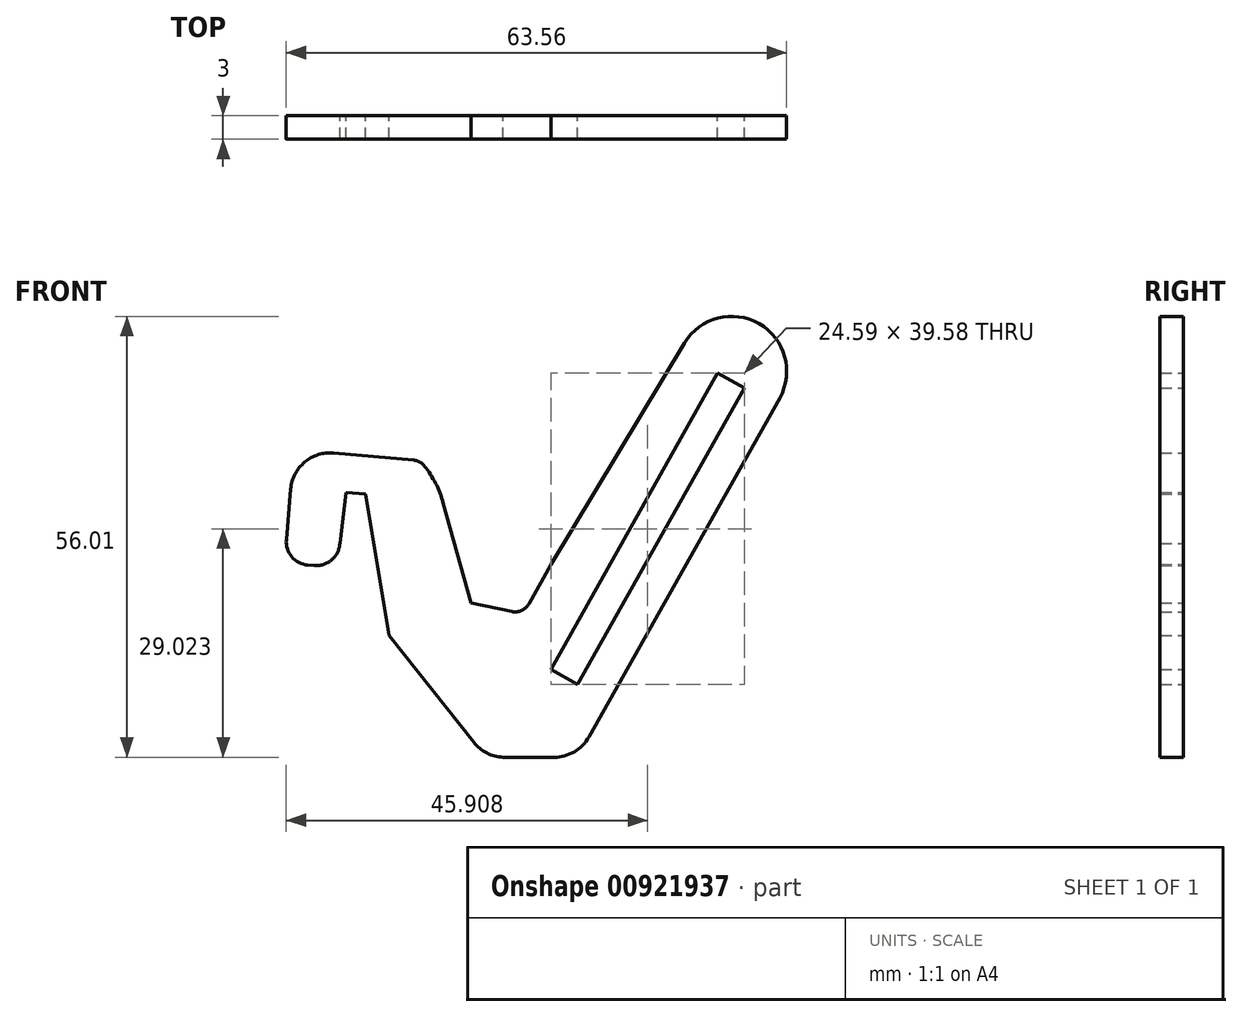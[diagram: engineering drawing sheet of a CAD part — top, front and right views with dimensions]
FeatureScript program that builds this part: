
annotation { "Feature Type Name" : "Feature", "Feature Type Description" : "" }
export const myFeature = defineFeature(function(context is Context, id is Id, definition is map)
    precondition{}
    {
        {
            var Q0;
            Q0=qCreatedBy(makeId("Front.planeOp"),FACE);
            var sketch = newSketch(context, id + "F0", { "sketchPlane" : qUnion([Q0])});
            skLineSegment(sketch, "E0", {"start": v(-27.5, 25.35) * mm, "end": v(-26.68, 25.28) * mm});
            skLineSegment(sketch, "E1", {"start": v(6.78, 10.17) * mm, "end": v(3.38, 12.08) * mm});
            skLineSegment(sketch, "E2", {"start": v(3.38, 12.08) * mm, "end": v(24.58, 49.74) * mm});
            skLineSegment(sketch, "E3", {"start": v(20.37, 53.56) * mm, "end": v(1.34, 22.02) * mm});
            skPoint(sketch, "E4.visualSharp", {"position": v(3.38, 25.4) * mm});
            skPoint(sketch, "E5.visualSharp", {"position": v(22.73, 46.46) * mm});
            skLineSegment(sketch, "E5.filletArc", {"start": v(24.58, 49.74) * mm, "end": v(24.58, 49.74) * mm});
            skPoint(sketch, "E6.visualSharp", {"position": v(27.2, 46.46) * mm});
            skLineSegment(sketch, "E6.filletArc", {"start": v(27.2, 46.46) * mm, "end": v(27.2, 46.46) * mm});
            skPoint(sketch, "E7.visualSharp", {"position": v(-21.33, 25.35) * mm});
            skArc(sketch, "E7.filletArc", {"start": v(-26.68, 25.28) * mm, "mid": v(-24.45, 26) * mm, "end": v(-23.43, 28.11) * mm});
            skLineSegment(sketch, "E8", {"start": v(3.38, 25.4) * mm, "end": v(0.58, 20.42) * mm});
            skLineSegment(sketch, "E9", {"start": v(-1.57, 19.44) * mm, "end": v(-6.79, 20.53) * mm});
            skPoint(sketch, "E10.visualSharp", {"position": v(-0.14, 19.14) * mm});
            skArc(sketch, "E10.filletArc", {"start": v(-1.57, 19.44) * mm, "mid": v(-0.34, 19.58) * mm, "end": v(0.58, 20.42) * mm});
            skPoint(sketch, "E11.visualSharp", {"position": v(-30.5, 25.35) * mm});
            skArc(sketch, "E11.filletArc", {"start": v(-30.22, 28.6) * mm, "mid": v(-29.53, 26.4) * mm, "end": v(-27.5, 25.35) * mm});
            skPoint(sketch, "E12.endSnap0", {"position": v(-22.65, 34.56) * mm});
            skLineSegment(sketch, "E13", {"start": v(-23.43, 28.11) * mm, "end": v(-22.65, 34.56) * mm});
            skLineSegment(sketch, "E14", {"start": v(-22.65, 34.56) * mm, "end": v(-20.15, 34.36) * mm});
            skLineSegment(sketch, "E15", {"start": v(-17.15, 16.4) * mm, "end": v(-6.4, 2.82) * mm});
            skLineSegment(sketch, "E16", {"start": v(-20.15, 34.36) * mm, "end": v(-17.15, 16.4) * mm});
            skPoint(sketch, "E17.visualSharp", {"position": v(-4.9, 0.93) * mm});
            skArc(sketch, "E17.filletArc", {"start": v(-6.4, 2.82) * mm, "mid": v(-4.75, 1.47) * mm, "end": v(-2.7, 0.93) * mm});
            skLineSegment(sketch, "E18", {"start": v(-24.24, 39.58) * mm, "end": v(-14.09, 38.69) * mm});
            skLineSegment(sketch, "E19", {"start": v(-29.65, 35.03) * mm, "end": v(-30.22, 28.6) * mm});
            skPoint(sketch, "E20.visualSharp", {"position": v(-30.5, 39.8) * mm});
            skArc(sketch, "E20.filletArc", {"start": v(-24.24, 39.58) * mm, "mid": v(-27.89, 38.43) * mm, "end": v(-29.65, 35.03) * mm});
            skPoint(sketch, "E21.visualSharp", {"position": v(-0.14, 38.58) * mm});
            skLineSegment(sketch, "E22", {"start": v(32.47, 46.59) * mm, "end": v(8.24, 3.53) * mm});
            skLineSegment(sketch, "E23", {"start": v(-2.7, 0.93) * mm, "end": v(3.8, 0.93) * mm});
            skPoint(sketch, "E24.visualSharp", {"position": v(6.78, 0.93) * mm});
            skArc(sketch, "E24.filletArc", {"start": v(3.8, 0.93) * mm, "mid": v(6.37, 1.62) * mm, "end": v(8.24, 3.53) * mm});
            skLineSegment(sketch, "E25.filletArc", {"start": v(32.4, 46.46) * mm, "end": v(32.4, 46.46) * mm});
            skArc(sketch, "E26", {"start": v(32.47, 46.6) * mm, "mid": v(29.83, 56) * mm, "end": v(20.37, 53.56) * mm});
            skLineSegment(sketch, "E27", {"start": v(24.58, 49.74) * mm, "end": v(27.97, 47.83) * mm});
            skPoint(sketch, "E28.endSnap0", {"position": v(29.8, 46.46) * mm});
            skArc(sketch, "E29.filletArc", {"start": v(32.47, 46.59) * mm, "mid": v(32.47, 46.6) * mm, "end": v(32.47, 46.6) * mm});
            skLineSegment(sketch, "E30", {"start": v(27.97, 47.83) * mm, "end": v(6.78, 10.17) * mm});
            skLineSegment(sketch, "E31", {"start": v(-6.79, 20.53) * mm, "end": v(-10.29, 33.24) * mm});
            skArc(sketch, "E32", {"start": v(-10.29, 33.24) * mm, "mid": v(-11.25, 35.72) * mm, "end": v(-12.7, 37.95) * mm});
            skPoint(sketch, "E33.visualSharp", {"position": v(-13.28, 38.62) * mm});
            skArc(sketch, "E33.filletArc", {"start": v(-12.7, 37.95) * mm, "mid": v(-13.32, 38.46) * mm, "end": v(-14.09, 38.69) * mm});
            skSolve(sketch);
        }
        {
            var Q0;
            Q0 = qSketchRegion(id + "F0", true);
            extrude(context, id + "F1", {"entities" : qUnion([Q0]), "depth" : 3 * mm, "offsetDistance" : 25 * mm});
        }
    });
